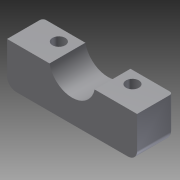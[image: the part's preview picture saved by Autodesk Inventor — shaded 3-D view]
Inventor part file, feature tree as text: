
AUTODESK INVENTOR PART (.ipt)
format: ipt  version: 2012 (Build 160160000, 160)  size: 161,792 bytes
history: native  units: mm
features: extrude x4, sketch x4, fillet x3
ambient origin geometry x8: Origin, YZ Plane, XZ Plane, XY Plane, X Axis, Y Axis, Z Axis, Center Point
bodies: Solid1 (feature_tree)
feature tree (11):
  extrude  "Extrusion1"  Depth=42.4mm
  extrude  "Extrusion2"  Depth=9.2mm
  fillet  "Fillet1"  Radius=9.2mm
  extrude  "Extrusion3"  Depth=9.2mm
  extrude  "Extrusion4"  Depth=4.0mm
  fillet  "Fillet3"  Radius=4.0mm
  fillet  "Fillet4"  Radius=4.0mm
  sketch  "Sketch1"  dims[d0=24.0mm d1=42.4mm]
  sketch  "Sketch2"  dims[d2=4.2mm d3=9.2mm d4=9.2mm]
  sketch  "Sketch3"  dims[d5=9.2mm d6=9.2mm]
  sketch  "Sketch4"  dims[d7=4.0mm d8=4.0mm d9=4.0mm d10=4.0mm d11=13.5mm d12=0.0mm d13=15.0mm d14=21.2mm d15=1.5mm d16=13.5mm d17=0.0mm d18=3.0mm d20=8.5mm d21=4.0mm d22=0.0mm d23=12.3mm d24=0.0mm d25=3.0mm d26=1.0mm]
